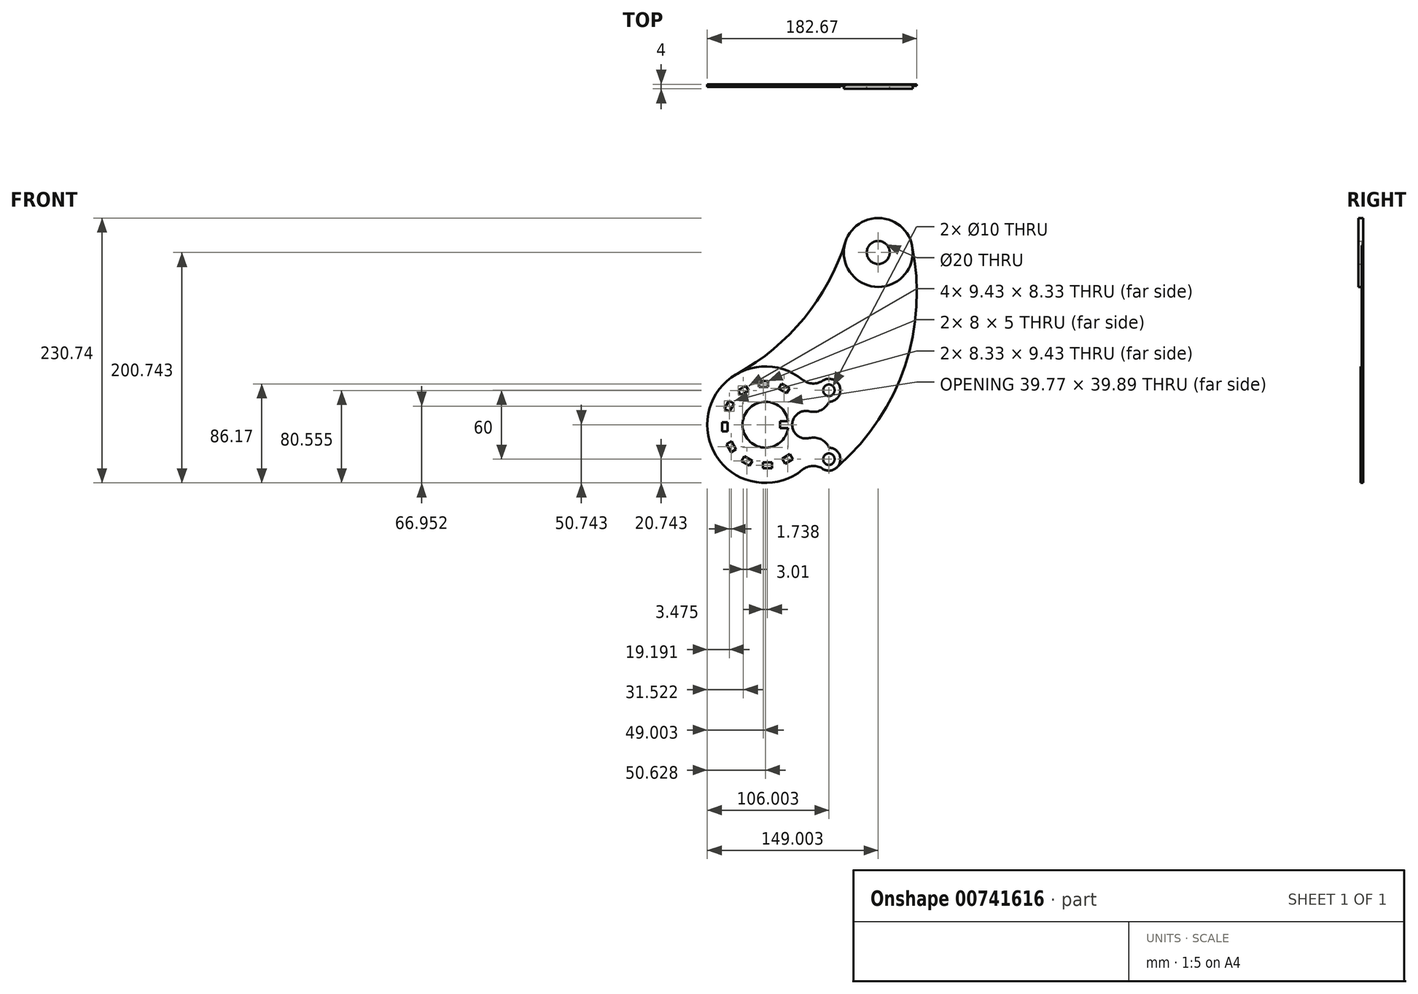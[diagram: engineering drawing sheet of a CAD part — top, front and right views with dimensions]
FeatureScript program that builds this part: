
annotation { "Feature Type Name" : "Feature", "Feature Type Description" : "" }
export const myFeature = defineFeature(function(context is Context, id is Id, definition is map)
    precondition{}
    {
        {
            var Q0;
            Q0=qCreatedBy(makeId("Front.planeOp"),FACE);
            var sketch = newSketch(context, id + "F0", { "sketchPlane" : qUnion([Q0])});
            skCircle(sketch, "E0", {"center": v(55.1, 114.57) * mm, "radius": 30 * mm});
            skArc(sketch, "E1", {"start": v(-23.4, -32.43) * mm, "mid": v(-63.17, -35.43) * mm, "end": v(-23.4, -38.43) * mm});
            skCircle(sketch, "E2", {"center": v(55.1, 114.57) * mm, "radius": 10 * mm});
            skCircle(sketch, "E3", {"center": v(12.1, -65.43) * mm, "radius": 5 * mm});
            skCircle(sketch, "E4", {"center": v(12.1, -5.43) * mm, "radius": 5 * mm});
            skLineSegment(sketch, "E5", {"start": v(-72.85, -35.43) * mm, "end": v(0, -35.43) * mm, "construction": true});
            skLineSegment(sketch, "E6", {"start": v(12.1, 5.32) * mm, "end": v(12.1, -3.64) * mm, "construction": true});
            skLineSegment(sketch, "E7", {"start": v(12.1, -39.77) * mm, "end": v(12.1, -59.4) * mm});
            skLineSegment(sketch, "E8", {"start": v(-44.9, 0) * mm, "end": v(-44.9, -72.35) * mm, "construction": true});
            skLineSegment(sketch, "E9", {"start": v(55.1, 75.2) * mm, "end": v(55.1, 157.47) * mm, "construction": true});
            skLineSegment(sketch, "E10", {"start": v(8.98, -5.43) * mm, "end": v(19.58, -5.43) * mm, "construction": true});
            skLineSegment(sketch, "E11", {"start": v(8.5, -65.43) * mm, "end": v(19.58, -65.43) * mm, "construction": true});
            skLineSegment(sketch, "E12", {"start": v(-23.4, -38.43) * mm, "end": v(-30.4, -38.43) * mm});
            skLineSegment(sketch, "E13", {"start": v(-30.4, -38.43) * mm, "end": v(-30.4, -32.43) * mm});
            skLineSegment(sketch, "E14", {"start": v(-30.4, -32.43) * mm, "end": v(-23.4, -32.43) * mm});
            skLineSegment(sketch, "E15", {"start": v(-5, 38.15) * mm, "end": v(-5, -80.02) * mm, "construction": true});
            skArc(sketch, "E16", {"start": v(12.3, -15.42) * mm, "mid": v(21.55, -2.18) * mm, "end": v(6.11, 2.59) * mm});
            skArc(sketch, "E17", {"start": v(6.11, -73.44) * mm, "mid": v(21.58, -68.58) * mm, "end": v(12.1, -55.43) * mm});
            skArc(sketch, "E18", {"start": v(-5, -23.78) * mm, "mid": v(-19.9, -35.43) * mm, "end": v(-5, -47.07) * mm});
            skArc(sketch, "E19", {"start": v(-5, -23.78) * mm, "mid": v(5.16, -22.74) * mm, "end": v(12.3, -15.42) * mm});
            skArc(sketch, "E20.MirrorCS", {"start": v(-5, -47.07) * mm, "mid": v(5.16, -48.12) * mm, "end": v(12.3, -55.43) * mm});
            skLineSegment(sketch, "E21", {"start": v(0, 31.33) * mm, "end": v(0, -83.41) * mm, "construction": true});
            skArc(sketch, "E22.trimOffspring", {"start": v(-11.06, 3.86) * mm, "mid": v(-93.91, -35.43) * mm, "end": v(-11.06, -74.71) * mm});
            skArc(sketch, "E23", {"start": v(-67.64, 9.02) * mm, "mid": v(-9.55, 57.29) * mm, "end": v(26.5, 123.66) * mm});
            skArc(sketch, "E24", {"start": v(20.22, -71.25) * mm, "mid": v(78.43, 16.03) * mm, "end": v(84.45, 120.77) * mm});
            skArc(sketch, "E25", {"start": v(-11.06, -74.71) * mm, "mid": v(-2.05, -71.34) * mm, "end": v(7.15, -74.12) * mm});
            skArc(sketch, "E26.MirrorCS", {"start": v(-11.06, 3.86) * mm, "mid": v(-2.05, 0.48) * mm, "end": v(7.15, 3.27) * mm});
            skLineSegment(sketch, "E27", {"start": v(-48.9, 2.5) * mm, "end": v(-40.9, 2.5) * mm});
            skLineSegment(sketch, "E28", {"start": v(-40.9, 2.5) * mm, "end": v(-40.9, -2.5) * mm});
            skLineSegment(sketch, "E29", {"start": v(-40.9, -2.5) * mm, "end": v(-48.9, -2.5) * mm});
            skLineSegment(sketch, "E30", {"start": v(-48.9, -2.5) * mm, "end": v(-48.9, 2.5) * mm});
            skLineSegment(sketch, "E31.1.0", {"start": v(-67.1, -5.45) * mm, "end": v(-60.17, -1.45) * mm});
            skLineSegment(sketch, "E31.1.1", {"start": v(-64.6, -9.78) * mm, "end": v(-67.1, -5.45) * mm});
            skLineSegment(sketch, "E31.1.2", {"start": v(-57.67, -5.78) * mm, "end": v(-64.6, -9.78) * mm});
            skLineSegment(sketch, "E31.1.3", {"start": v(-60.17, -1.45) * mm, "end": v(-57.67, -5.78) * mm});
            skLineSegment(sketch, "E31.2.0", {"start": v(-78.88, -21.43) * mm, "end": v(-74.88, -14.5) * mm});
            skLineSegment(sketch, "E31.2.1", {"start": v(-74.55, -23.93) * mm, "end": v(-78.88, -21.43) * mm});
            skLineSegment(sketch, "E31.2.2", {"start": v(-70.55, -17) * mm, "end": v(-74.55, -23.93) * mm});
            skLineSegment(sketch, "E31.2.3", {"start": v(-74.88, -14.5) * mm, "end": v(-70.55, -17) * mm});
            skLineSegment(sketch, "E31.3.0", {"start": v(-81.1, -41.16) * mm, "end": v(-81.1, -33.16) * mm});
            skLineSegment(sketch, "E31.3.1", {"start": v(-76.1, -41.16) * mm, "end": v(-81.1, -41.16) * mm});
            skLineSegment(sketch, "E31.3.2", {"start": v(-76.1, -33.16) * mm, "end": v(-76.1, -41.16) * mm});
            skLineSegment(sketch, "E31.3.3", {"start": v(-81.1, -33.16) * mm, "end": v(-76.1, -33.16) * mm});
            skLineSegment(sketch, "E31.4.0", {"start": v(-73.15, -59.36) * mm, "end": v(-77.15, -52.43) * mm});
            skLineSegment(sketch, "E31.4.1", {"start": v(-68.82, -56.86) * mm, "end": v(-73.15, -59.36) * mm});
            skLineSegment(sketch, "E31.4.2", {"start": v(-72.82, -49.93) * mm, "end": v(-68.82, -56.86) * mm});
            skLineSegment(sketch, "E31.4.3", {"start": v(-77.15, -52.43) * mm, "end": v(-72.82, -49.93) * mm});
            skLineSegment(sketch, "E31.5.0", {"start": v(-57.16, -71.14) * mm, "end": v(-64.1, -67.14) * mm});
            skLineSegment(sketch, "E31.5.1", {"start": v(-54.66, -66.81) * mm, "end": v(-57.16, -71.14) * mm});
            skLineSegment(sketch, "E31.5.2", {"start": v(-61.6, -62.81) * mm, "end": v(-54.66, -66.81) * mm});
            skLineSegment(sketch, "E31.5.3", {"start": v(-64.1, -67.14) * mm, "end": v(-61.6, -62.81) * mm});
            skLineSegment(sketch, "E31.6.0", {"start": v(-37.43, -73.35) * mm, "end": v(-45.43, -73.35) * mm});
            skLineSegment(sketch, "E31.6.1", {"start": v(-37.43, -68.35) * mm, "end": v(-37.43, -73.35) * mm});
            skLineSegment(sketch, "E31.6.2", {"start": v(-45.43, -68.35) * mm, "end": v(-37.43, -68.35) * mm});
            skLineSegment(sketch, "E31.6.3", {"start": v(-45.43, -73.35) * mm, "end": v(-45.43, -68.35) * mm});
            skLineSegment(sketch, "E31.7.0", {"start": v(-19.24, -65.4) * mm, "end": v(-26.17, -69.4) * mm});
            skLineSegment(sketch, "E31.7.1", {"start": v(-21.74, -61.07) * mm, "end": v(-19.24, -65.4) * mm});
            skLineSegment(sketch, "E31.7.2", {"start": v(-28.67, -65.07) * mm, "end": v(-21.74, -61.07) * mm});
            skLineSegment(sketch, "E31.7.3", {"start": v(-26.17, -69.4) * mm, "end": v(-28.67, -65.07) * mm});
            skLineSegment(sketch, "E31.11.0", {"start": v(-29.17, 0.29) * mm, "end": v(-22.25, -3.71) * mm});
            skLineSegment(sketch, "E31.11.1", {"start": v(-31.67, -4.04) * mm, "end": v(-29.17, 0.29) * mm});
            skLineSegment(sketch, "E31.11.2", {"start": v(-24.75, -8.04) * mm, "end": v(-31.67, -4.04) * mm});
            skLineSegment(sketch, "E31.11.3", {"start": v(-22.25, -3.71) * mm, "end": v(-24.75, -8.04) * mm});
            skPoint(sketch, "E32.orphan", {"position": v(-10.24, -29.69) * mm});
            skSolve(sketch);
        }
        {
            var Q0;
            Q0=makeQuery(id+"F0.imprint","IMPRINT",FACE,{"disambiguationData":[TD([[makeQuery(id+"F0.imprint","IMPRINT",EDGE,{"derivedFrom":sQuery(id+"F0.wireOp",EDGE,"E1")}),-1.0]])]});
            extrude(context, id + "F1", {"entities" : qUnion([Q0]), "depth" : 2.3 * mm, "offsetDistance" : 25 * mm});
        }
        {
            var Q0;
            Q0=makeQuery(id+"F0.imprint","IMPRINT",FACE,{"disambiguationData":[TD([[makeQuery(id+"F0.imprint","IMPRINT",EDGE,{"derivedFrom":sQuery(id+"F0.wireOp",EDGE,"E2")}),-1.0]])]});
            extrude(context, id + "F2", {"entities" : qUnion([Q0]), "depth" : 4 * mm, "offsetDistance" : 25 * mm});
        }
        {
            var Q0;
            {var subQ8=sQuery(id+"F0.wireOp",EDGE,"E18");Q0=makeQuery(id+"F0.imprint","IMPRINT",FACE,{"disambiguationData":[TD([[makeQuery(id+"F0.imprint","IMPRINT",EDGE,{"derivedFrom":subQ8}),1.0]])]});}
            extrude(context, id + "F3", {"entities" : qUnion([Q0]), "depth" : 1.2 * mm, "offsetDistance" : 25 * mm});
        }
    });
